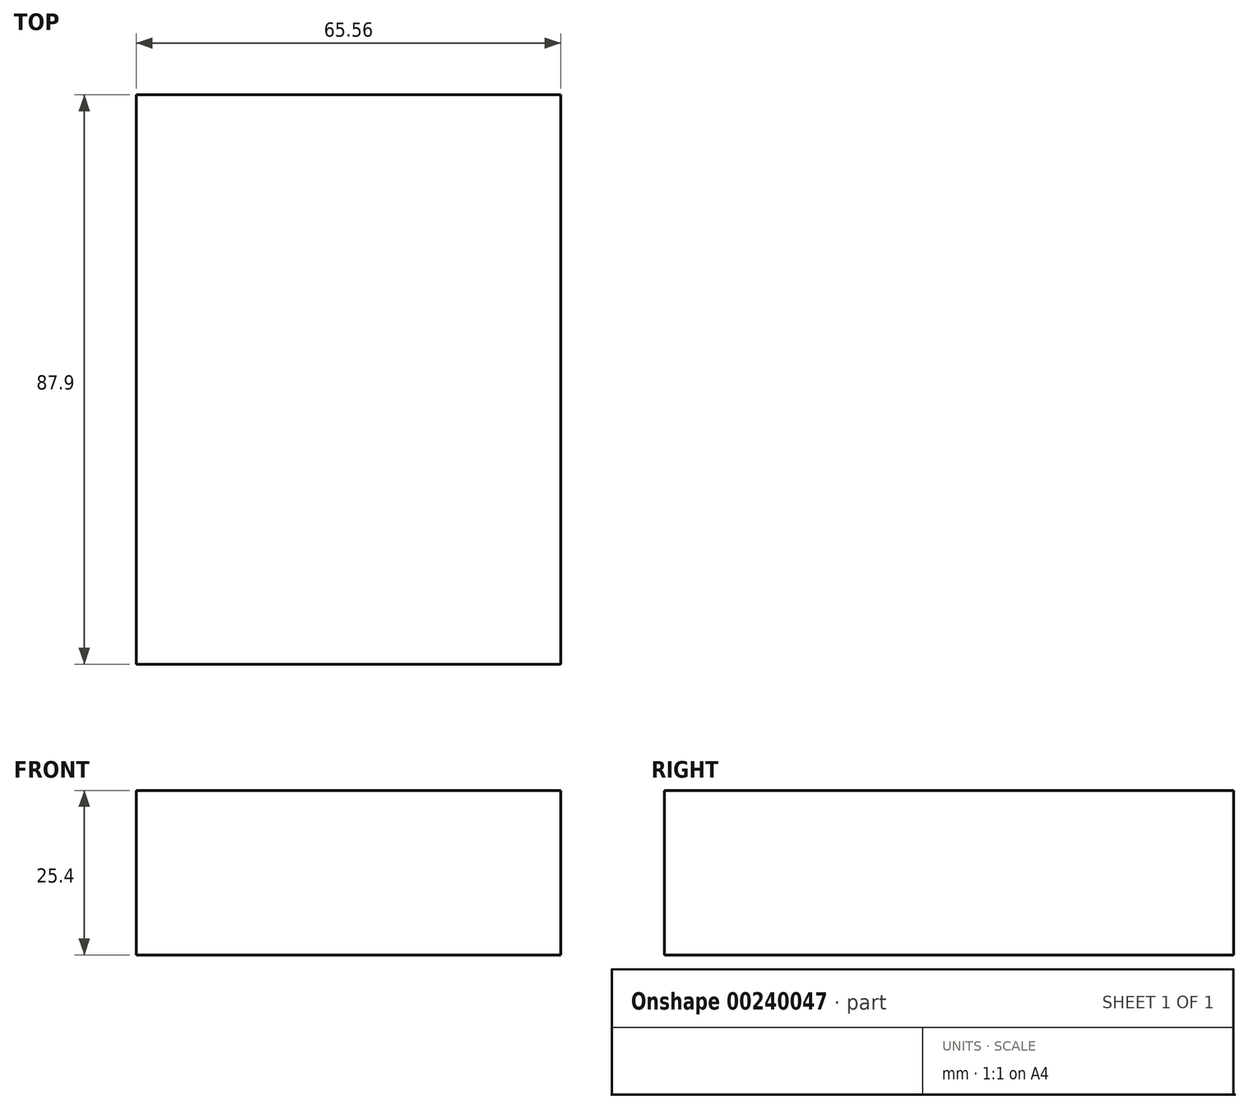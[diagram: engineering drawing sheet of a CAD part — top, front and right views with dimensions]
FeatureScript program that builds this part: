
annotation { "Feature Type Name" : "Feature", "Feature Type Description" : "" }
export const myFeature = defineFeature(function(context is Context, id is Id, definition is map)
    precondition{}
    {
        {
            var Q0;
            Q0=qCreatedBy(makeId("Top.planeOp"),FACE);
            var sketch = newSketch(context, id + "F0", { "sketchPlane" : qUnion([Q0])});
            skLineSegment(sketch, "E0.bottom", {"start": v(32.78, -43.95) * mm, "end": v(-32.78, -43.95) * mm});
            skLineSegment(sketch, "E0.top", {"start": v(32.78, 43.95) * mm, "end": v(-32.78, 43.95) * mm});
            skLineSegment(sketch, "E0.left", {"start": v(32.78, -43.95) * mm, "end": v(32.78, 43.95) * mm});
            skLineSegment(sketch, "E0.right", {"start": v(-32.78, -43.95) * mm, "end": v(-32.78, 43.95) * mm});
            skPoint(sketch, "E0.middle", {"position": v(0, 0) * mm});
            skSolve(sketch);
        }
        {
            var Q0;
            Q0=makeQuery(id+"F0.imprint","IMPRINT",FACE,{"disambiguationData":[TD([[makeQuery(id+"F0.imprint","IMPRINT",EDGE,{"derivedFrom":sQuery(id+"F0.wireOp",EDGE,"E0.bottom")}),-1.0]])]});
            extrude(context, id + "F1", {"entities" : qUnion([Q0]), "depth" : 25.4 * mm});
        }
    });
